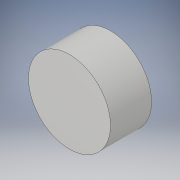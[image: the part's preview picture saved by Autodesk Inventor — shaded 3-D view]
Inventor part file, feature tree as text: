
AUTODESK INVENTOR PART (.ipt)
format: ipt  version: 2018 (Build 220112000, 112)  size: 110,592 bytes
history: native  units: mm
features: other x1, sketch x1
ambient origin geometry x8: Origin, YZ Plane, XZ Plane, XY Plane, X Axis, Y Axis, Z Axis, Center Point
bodies: Body1 (feature_tree)
feature tree (2):
  other  "reifen_felge"
  sketch  "Skizze1"  dims[d0=40.0mm d4=20.0mm d5=0.0mm]
